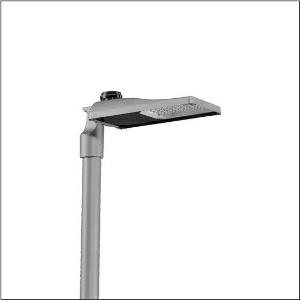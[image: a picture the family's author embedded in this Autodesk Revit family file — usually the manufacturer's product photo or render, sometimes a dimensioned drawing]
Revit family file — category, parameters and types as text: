
# Revit family: streetlight_sl_31_mini___st1_0a_5xh2d3bn08ha_f2e6
name_source: partatom
category: Lighting Fixtures
units: mm (PartAtom-declared; Revit-internal decimal feet)

## family parameters
Cut with Voids When Loaded = No
Host = Face
Light Source = No
Part Type = Normal
Room Calculation Point = No
Round Connector Dimension = Use Diameter
Shared = No

## types (1)
- --- (1 x LED, 9240 lm, 68.3 W, 3000K)
    Apparent Load = 68 VA
    CIE Flux Codes = 37 72 97 100 100
    Color Rendering = 70
    Color Temperature = 3000K
    Default Elevation = 1800 mm
    Description = Streetlight SL 31 mini NEMA (7pin) mast luminaire for post-top, side-entry; light control with lens of PMMA; light distribution: ST1.0a, direct asymmetric distribution, for standard-compliant lighting for roads and squares; LED: luminous flux: 9.240lm, light colour: 730, colour temperature: 3000K; luminous efficacy: 135,3lm/W; control: overheat protection, intelligent temperature release in ECG and LED module, constant luminous flux control, time-dependent luminous flux control, flexible luminous flux parameterisation, pre-setting: linear dimming characteristic; luminaire housing, of diecast aluminium, SITECO metallic grey (DB 702S), corrosivity category C5 high according to DIN EN ISO 12944; cover of toughened safety glass, transparent, mast flange of diecast aluminium, SITECO metallic grey (DB 702S), spigot size: 76/60mm, mast flange included unmounted; cable length: 8,5m, connection cable pre-assembled; mains connection: 220..240V, AC, 50/60Hz; power consumption (at start of service life): 68,3W / (at end of service life): 74,8W / (with reduced operation 50%): 29,7W; protection rating (complete): IP66; insulation class (complete): insulation class I (protective earthing); impact resistance: IK10; certification: CE, ENEC, ENEC+, VDE, UKCA; permissible operating ambient temperature for outdoor applications: -40..+50°C; packaging unit: 1 piece

Light Distribution: ST1.0a
    Height = 76 mm
    Lamp = 1 x LED
    Lamp Light Flux = 9240 lm
    Lamp Power = 68.3 W
    Lamp count = 1
    Length = 547 mm
    Luminous efficacy = 135 lm/W
    Manufacturer = Siteco
    ModVariant = No
    Model = 5XH2D3BN08HA
    Number of Poles = 1
    OnlyDefault = Yes
    Power Factor = 1
    Product Name = Streetlight SL 31 mini | ST1.0a
    Product group = mast luminaire | pylon top
    ProductGroupID = 6100
    Protection Class = Protection class I
    Protection Degree = IP 66
    RLX_Detail_Level = 1
    RLX_Emergency_Light_Flux = 0 lm
    RLX_Emergency_Type = 0
    RLX_Emergency_Type_DB = No
    RlxData = <blob elided: 39929 chars, md5=931dc58f>
    Socket = socket
    Standby Power = 0 W
    System Light Flux = 9240 lm
    System Power = 68 W
    Type Comments = factory setting: luminous flux: 100 % | dim-lin: 254 | 693 mA
    Type Image = l_1300322.jpg
    URL = http://relux.com
    VarID = @adj_061217
    Voltage = 0 V
    Weight = 0.00 kg
    Width = 265 mm

## geometry (parser evidence)
native form markers: Blend x4, Sweep x10
no freeform markers — native parametric forms only
